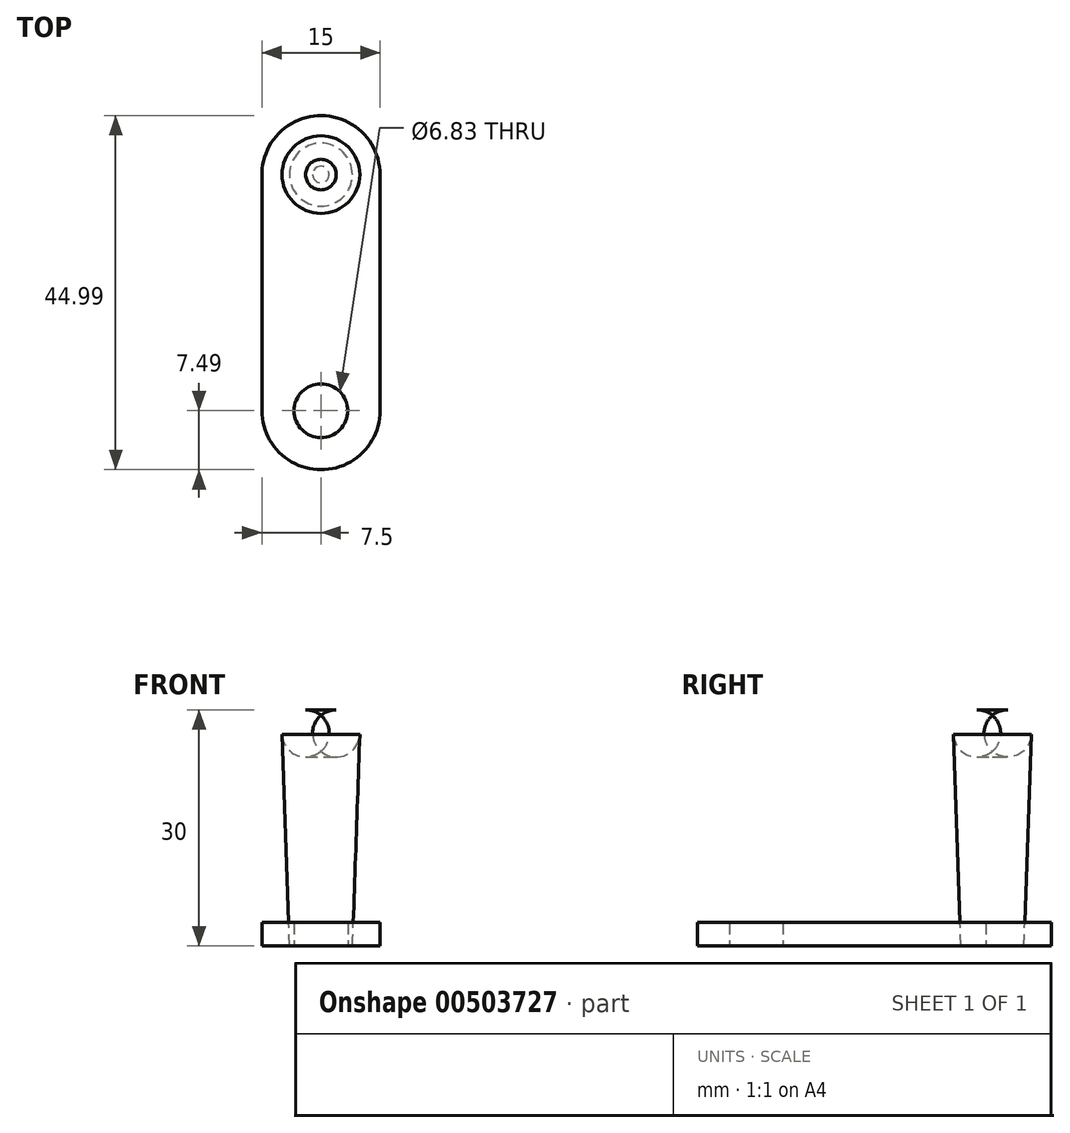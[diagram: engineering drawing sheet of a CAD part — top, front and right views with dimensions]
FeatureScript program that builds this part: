
annotation { "Feature Type Name" : "Feature", "Feature Type Description" : "" }
export const myFeature = defineFeature(function(context is Context, id is Id, definition is map)
    precondition{}
    {
        {
            var Q0;
            Q0=qCreatedBy(makeId("Top.planeOp"),FACE);
            var sketch = newSketch(context, id + "F0", { "sketchPlane" : qUnion([Q0])});
            skCircle(sketch, "E0", {"center": v(0, 0) * mm, "radius": 3.41 * mm});
            skLineSegment(sketch, "E1", {"start": v(-7.45, 30.82) * mm, "end": v(-7.5, 0) * mm});
            skLineSegment(sketch, "E2", {"start": v(7.5, 0) * mm, "end": v(7.5, 30) * mm});
            skArc(sketch, "E3", {"start": v(-7.45, 30.82) * mm, "mid": v(-7.5, 30.01) * mm, "end": v(-7.46, 29.2) * mm});
            skArc(sketch, "E4", {"start": v(7.5, 30) * mm, "mid": v(0.41, 37.49) * mm, "end": v(-7.45, 30.82) * mm});
            skArc(sketch, "E5", {"start": v(-7.5, 0.01) * mm, "mid": v(0, -7.5) * mm, "end": v(7.5, 0) * mm});
            skCircle(sketch, "E6", {"center": v(0, 30) * mm, "radius": 4 * mm});
            skSolve(sketch);
        }
        {
            var Q0;
            Q0 = qSketchRegion(id + "F0", true);
            var Q1;
            Q1=makeQuery(id+"F0.imprint","IMPRINT",FACE,{"disambiguationData":[TD([[makeQuery(id+"F0.imprint","IMPRINT",EDGE,{"derivedFrom":sQuery(id+"F0.wireOp",EDGE,"E6")}),1.0]])]});
            extrude(context, id + "F1", {"entities" : qUnion([Q0, Q1]), "depth" : 3 * mm});
        }
        {
            var Q0;
            Q0=makeQuery(id+"F0.imprint","IMPRINT",FACE,{"disambiguationData":[TD([[makeQuery(id+"F0.imprint","IMPRINT",EDGE,{"derivedFrom":sQuery(id+"F0.wireOp",EDGE,"E6")}),1.0]])]});
            var Q1;
            Q1=sQuery(id+"F0.wireOp",EDGE,"E6");
            extrude(context, id + "F2", {"entities" : qUnion([Q0]), "surfaceEntities" : qUnion([Q1]), "depth" : 30 * mm, "hasDraft" : true, "draftAngle" : 2 * degree});
        }
        {
            var Q0;
            Q0=makeQuery(id+"F2.opExtrude","CAP_EDGE",EDGE,{"disambiguationData":[OSD([sQuery(id+"F0.wireOp",EDGE,"E6")])],"isStart":false});
            fillet(context, id + "F3", {"entities" : qUnion([Q0]), "radius" : 3 * mm, "tangentPropagation" : true, "allowEdgeOverflow" : false});
        }
    });
